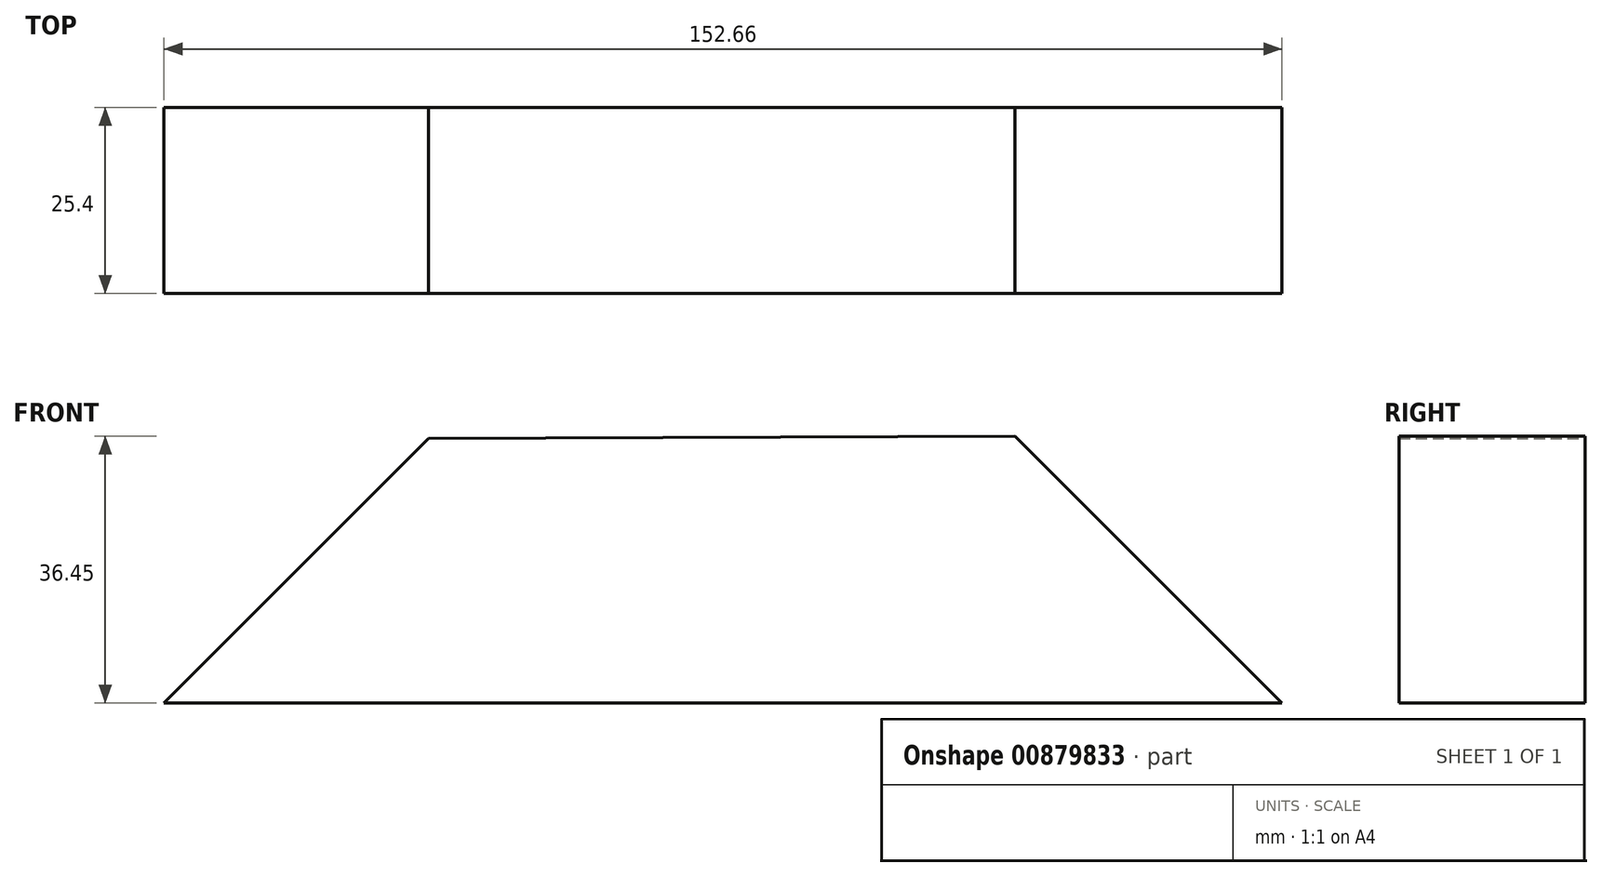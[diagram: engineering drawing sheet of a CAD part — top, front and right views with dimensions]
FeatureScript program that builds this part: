
annotation { "Feature Type Name" : "Feature", "Feature Type Description" : "" }
export const myFeature = defineFeature(function(context is Context, id is Id, definition is map)
    precondition{}
    {
        {
            var Q0;
            Q0=qCreatedBy(makeId("Front.planeOp"),FACE);
            var sketch = newSketch(context, id + "F0", { "sketchPlane" : qUnion([Q0])});
            skLineSegment(sketch, "E0", {"start": v(-62.23, -26.2) * mm, "end": v(90.43, -26.2) * mm});
            skLineSegment(sketch, "E1", {"start": v(-62.23, -26.2) * mm, "end": v(-26.1, 9.94) * mm});
            skLineSegment(sketch, "E2", {"start": v(90.43, -26.2) * mm, "end": v(53.97, 10.25) * mm});
            skLineSegment(sketch, "E3", {"start": v(-26.1, 9.94) * mm, "end": v(53.97, 10.25) * mm});
            skSolve(sketch);
        }
        {
            var Q0;
            Q0 = qSketchRegion(id + "F0", true);
            extrude(context, id + "F1", {"entities" : qUnion([Q0]), "depth" : 25.4 * mm, "offsetDistance" : 25.4 * mm});
        }
    });
